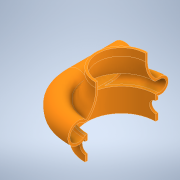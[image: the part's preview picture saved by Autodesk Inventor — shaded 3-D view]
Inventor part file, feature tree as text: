
AUTODESK INVENTOR PART (.ipt)
format: ipt  version: 2022 (Build 260153000, 153)  size: 738,304 bytes
history: native  units: mm
features: sketch x18, extrude x10, plane x4, revolve x3, loft x1, fillet x1
ambient origin geometry x8: Origin, YZ Plane, XZ Plane, XY Plane, X Axis, Y Axis, Z Axis, Center Point
bodies: Solid1 (feature_tree)
feature tree (37):
  sketch  "Sketch1"  dims[d0=65.0mm d1=41.0mm]
  sketch  "Sketch2"  dims[d2=20.5mm d3=0.0mm d4=20.5mm d5=3.5mm d10=3.0mm]
  revolve  "Revolution1"  [1 undecoded]
  sketch  "Sketch5"  dims[d19=7.0mm d22=20.0mm]
  plane  "Work Plane2"
  sketch  "Sketch8"  dims[d23=6.5mm d27=14.5mm]
  plane  "Work Plane4"
  plane  "Work Plane6"
  sketch  "Sketch12"  dims[d30=18.188mm d31=1.5mm]
  loft  "Loft2"
  extrude  "Extrusion2"  TaperAngle=0.0deg  [1 undecoded]
  revolve  "Revolution3"  [1 undecoded]
  revolve  "Revolution4"  [1 undecoded]
  sketch  "Sketch21"  dims[d46=4.5mm d47=3.5mm]
  extrude  "Extrusion4"  Depth=0.5mm
  extrude  "Extrusion5"  Depth=1.5mm
  sketch  "Sketch22"  dims[d48=3.0mm d49=-4.75mm]
  plane  "Work Plane8"
  extrude  "Extrusion6"  Depth=0.5mm
  fillet  "Fillet1"  Radius=7.6mm
  extrude  "Extrusion7"  Depth=5.0mm
  extrude  "Extrusion8"  Depth=3.5mm
  extrude  "Extrusion10"  [1 undecoded]
  extrude  "Extrusion11"  Depth=24.0mm
  extrude  "Extrusion12"  Depth=12.5mm
  extrude  "Extrusion13"  TaperAngle=0.0deg  [1 undecoded]
  sketch  "Sketch3"  dims[d11=2.6mm d13=0.0mm]
  sketch  "Sketch9"  dims[d28=14.0mm d29=0.5mm]
  sketch  "Sketch17"  dims[d33=1.0mm d34=0.5mm d35=7.6mm]
  sketch  "Sketch18"  dims[d36=360.0deg d45=5.0mm]
  sketch  "Sketch23"  dims[d50=27.0mm d51=24.0mm]
  sketch  "Sketch24"  dims[d65=15.0mm d66=12.5mm]
  sketch  "Sketch25"  dims[d67=0.0mm d68=90.0deg d69=0.0mm d70=90.0deg]
  sketch  "Sketch29"  dims[d71=0.0mm d72=90.0deg]
  sketch  "Sketch30"  dims[d80=12.5mm]
  sketch  "Sketch31"  dims[d81=15.0mm]
  sketch  "Sketch32"  dims[d82=28.8mm d83=0.0mm d84=360.0deg d85=22.0mm d86=90.0deg d89=2.5mm d90=0.0mm d91=10.0mm d92=0.0mm d93=5.0mm d94=0.0mm d95=0.1mm d96=42.0mm d97=2.0mm d98=0.0mm d99=0.2mm d103=0.2mm d104=42.0mm d105=45.0mm d106=13.0mm d107=0.0mm d119=10.0mm d120=0.0mm d121=3.0mm d122=0.0mm d123=7.0mm d124=7.05mm d125=0.0mm d126=0.0mm d127=13.0mm d128=0.0mm]
note: 6 required parameter values undecoded (feature->parameter linkage not recoverable at this tier; creation-order binding heuristic only, values carry confidence <= 0.55)